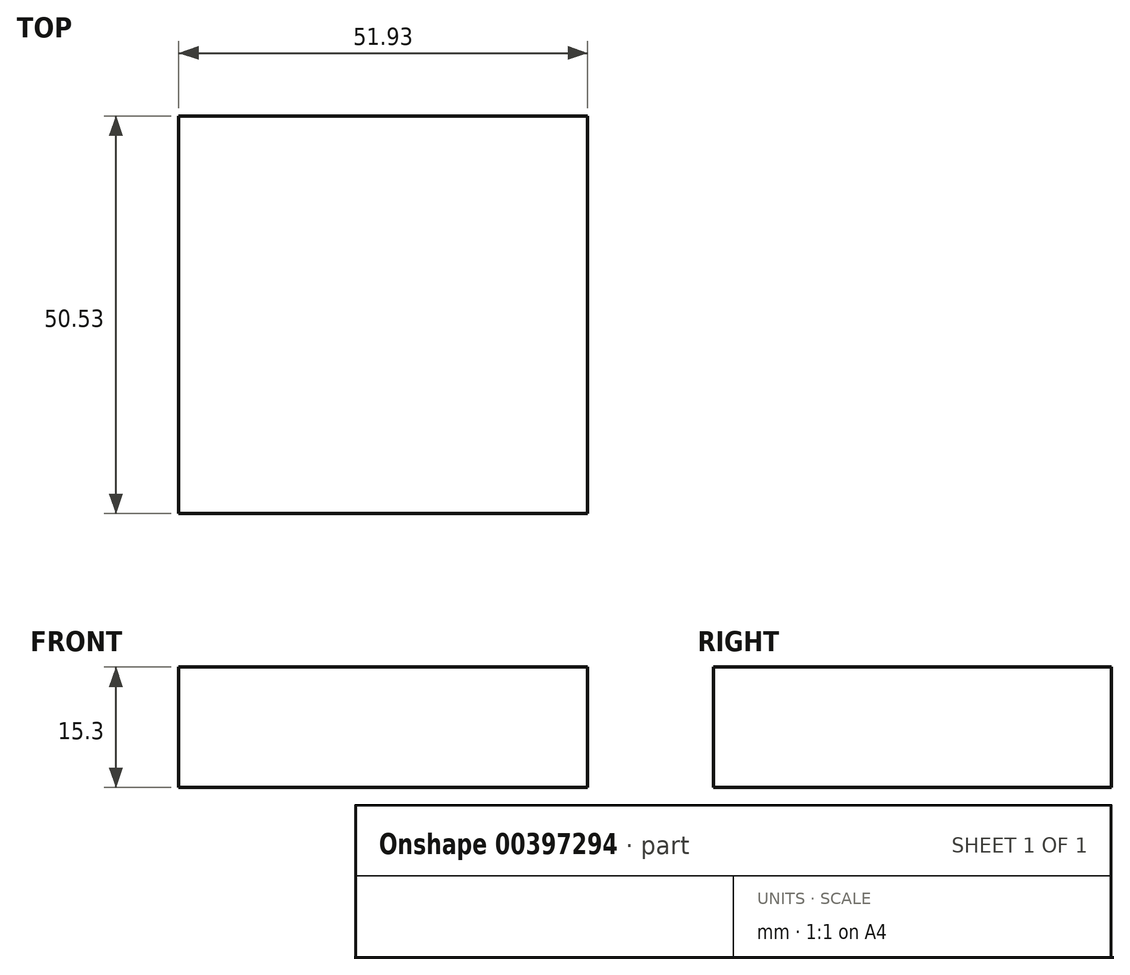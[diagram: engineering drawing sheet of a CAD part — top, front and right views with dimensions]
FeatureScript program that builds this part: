
annotation { "Feature Type Name" : "Feature", "Feature Type Description" : "" }
export const myFeature = defineFeature(function(context is Context, id is Id, definition is map)
    precondition{}
    {
        {
            var Q0;
            Q0=qCreatedBy(makeId("Top.planeOp"),FACE);
            var sketch = newSketch(context, id + "F0", { "sketchPlane" : qUnion([Q0])});
            skLineSegment(sketch, "E0", {"start": v(0, 0) * mm, "end": v(51.93, 0) * mm});
            skLineSegment(sketch, "E1", {"start": v(51.93, 0) * mm, "end": v(51.93, 50.53) * mm});
            skLineSegment(sketch, "E2", {"start": v(51.93, 50.53) * mm, "end": v(0, 50.53) * mm});
            skLineSegment(sketch, "E3", {"start": v(0, 50.53) * mm, "end": v(0, 0) * mm});
            skSolve(sketch);
        }
        {
            var Q0;
            Q0 = qSketchRegion(id + "F0", true);
            extrude(context, id + "F1", {"entities" : qUnion([Q0]), "depth" : 15.3 * mm});
        }
    });
